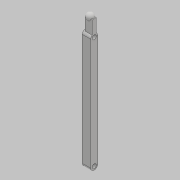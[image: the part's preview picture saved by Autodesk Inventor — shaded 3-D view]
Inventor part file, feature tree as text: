
AUTODESK INVENTOR PART (.ipt)
format: ipt  version: 2018 (Build 220112000, 112)  size: 163,840 bytes
history: native  units: mm
features: sketch x8, extrude x6, other x5, plane x5, fillet x2, hole x2, projected_geometry x2, mirror x1
ambient origin geometry x8: Origin, YZ Plane, XZ Plane, XY Plane, X Axis, Y Axis, Z Axis, Center Point
bodies: Body1 (feature_tree)
feature tree (31):
  other  "實體1"
  extrude  "擠出1"  Depth=5.0mm
  fillet  "圓角1"  Radius=85.0mm
  hole  "孔1"  [1 undecoded]
  fillet  "圓角2"  Radius=2.5mm
  hole  "孔2"  [1 undecoded]
  extrude  "擠出2"  Depth=2.5mm
  plane  "工作平面1"
  extrude  "擠出3"  Depth=10.0mm
  other  "迴轉1"
  other  "工作軸線1"
  plane  "工作平面3"
  mirror  "鏡射1"
  extrude  "擠出4"  Depth=3.0mm
  extrude  "擠出5"  Depth=16.0mm
  extrude  "擠出6"  Depth=5.0mm TaperAngle=0.0deg
  plane  "工作平面5"
  other  "迴轉2"
  sketch  "草圖1"
  sketch  "草圖2"
  projected_geometry  "投影迴路1"
  sketch  "草圖3"
  sketch  "草圖4"
  other  "工作軸線2"
  plane  "工作平面2"
  plane  "工作平面4"
  sketch  "草圖5"
  projected_geometry  "投影迴路2"
  sketch  "草圖6"
  sketch  "草圖7"
  sketch  "草圖8"
note: 2 required parameter values undecoded (feature->parameter linkage not recoverable at this tier; creation-order binding heuristic only, values carry confidence <= 0.55)
